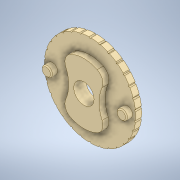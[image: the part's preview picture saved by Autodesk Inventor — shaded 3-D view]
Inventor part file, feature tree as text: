
AUTODESK INVENTOR PART (.ipt)
format: ipt  version: 2022 (Build 260153000, 153)  size: 225,280 bytes
history: native  units: mm
features: extrude x3, sketch x2, other x1, fillet x1, chamfer x1, pattern_circular x1
ambient origin geometry x8: Origin, YZ Plane, XZ Plane, XY Plane, X Axis, Y Axis, Z Axis, Center Point
bodies: Body1 (feature_tree)
feature tree (9):
  other  "Sólido1"
  sketch  "Esboço1"  dims[d0=20.0mm d1=60.0mm]
  extrude  "Extrusão1"  Depth=20.0mm
  extrude  "Extrusão2"  Depth=12.0mm
  fillet  "Arredondamento1"  Radius=50.0mm
  chamfer  "Chanfro1"  Distance=70.0mm
  extrude  "Extrusão3"  Depth=50.0mm
  pattern_circular  "Padrão circular1"  [2 undecoded]
  sketch  "Esboço2"  dims[d2=70.0mm d3=90.0mm d4=50.0mm d5=70.0mm d6=50.0mm d7=10.0mm d8=10.0mm d9=74.0mm d10=37.0mm d16=6.0mm d17=0.0mm d18=12.0mm d19=0.0mm d20=10.0mm d21=1.0mm d22=2.0mm d23=45.0deg d24=2.0mm d25=12.0mm d26=0.0mm d27=300.0mm d28=360.0deg]
note: 2 required parameter values undecoded (feature->parameter linkage not recoverable at this tier; creation-order binding heuristic only, values carry confidence <= 0.55)
